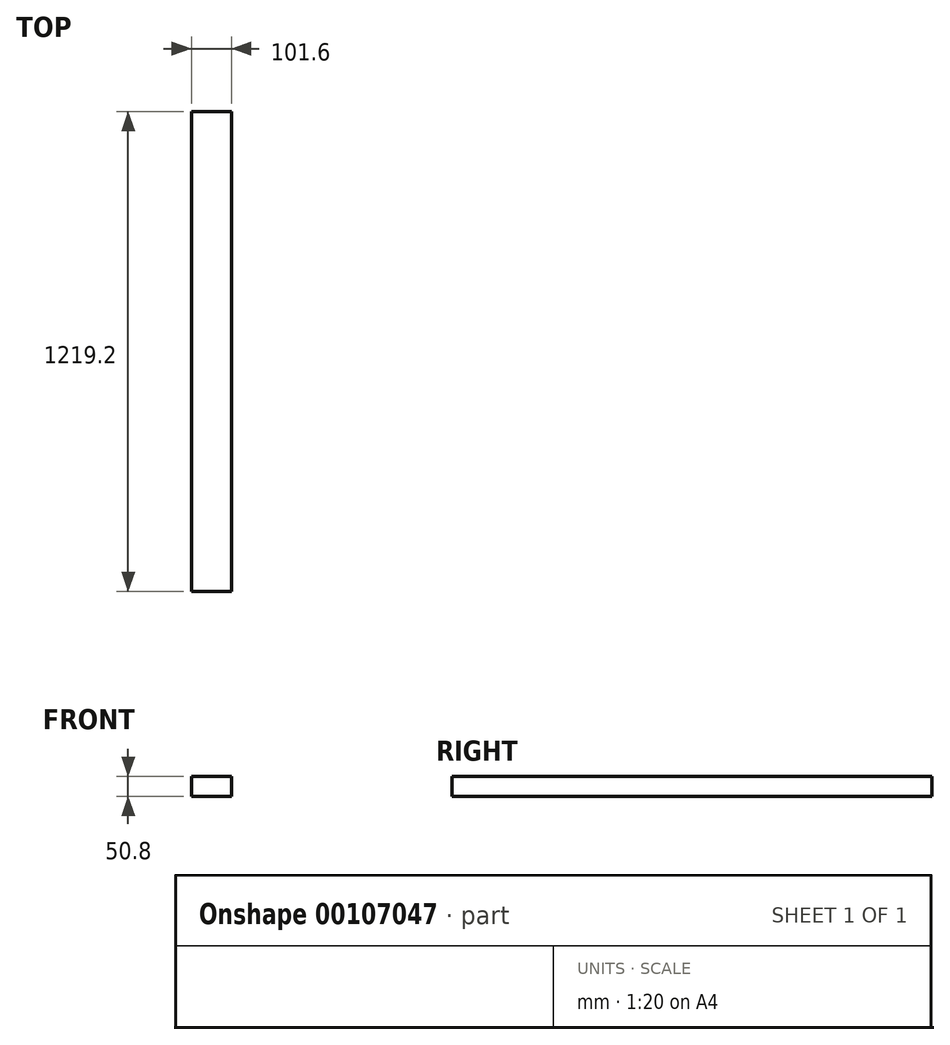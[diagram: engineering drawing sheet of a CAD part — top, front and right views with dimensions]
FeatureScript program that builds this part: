
annotation { "Feature Type Name" : "Feature", "Feature Type Description" : "" }
export const myFeature = defineFeature(function(context is Context, id is Id, definition is map)
    precondition{}
    {
        {
            var Q0;
            Q0=qCreatedBy(makeId("Top.planeOp"),FACE);
            var sketch = newSketch(context, id + "F0", { "sketchPlane" : qUnion([Q0])});
            skLineSegment(sketch, "E0.bottom", {"start": v(-77.2, 1160.44) * mm, "end": v(24.4, 1160.44) * mm});
            skLineSegment(sketch, "E0.top", {"start": v(-77.2, -58.76) * mm, "end": v(24.4, -58.76) * mm});
            skLineSegment(sketch, "E0.left", {"start": v(-77.2, 1160.44) * mm, "end": v(-77.2, -58.76) * mm});
            skLineSegment(sketch, "E0.right", {"start": v(24.4, 1160.44) * mm, "end": v(24.4, -58.76) * mm});
            skSolve(sketch);
        }
        {
            var Q0;
            Q0=makeQuery(id+"F0.imprint","IMPRINT",FACE,{"disambiguationData":[TD([[makeQuery(id+"F0.imprint","IMPRINT",EDGE,{"derivedFrom":sQuery(id+"F0.wireOp",EDGE,"E0.bottom")}),-1.0]])]});
            extrude(context, id + "F1", {"entities" : qUnion([Q0]), "depth" : 50.8 * mm});
        }
    });
